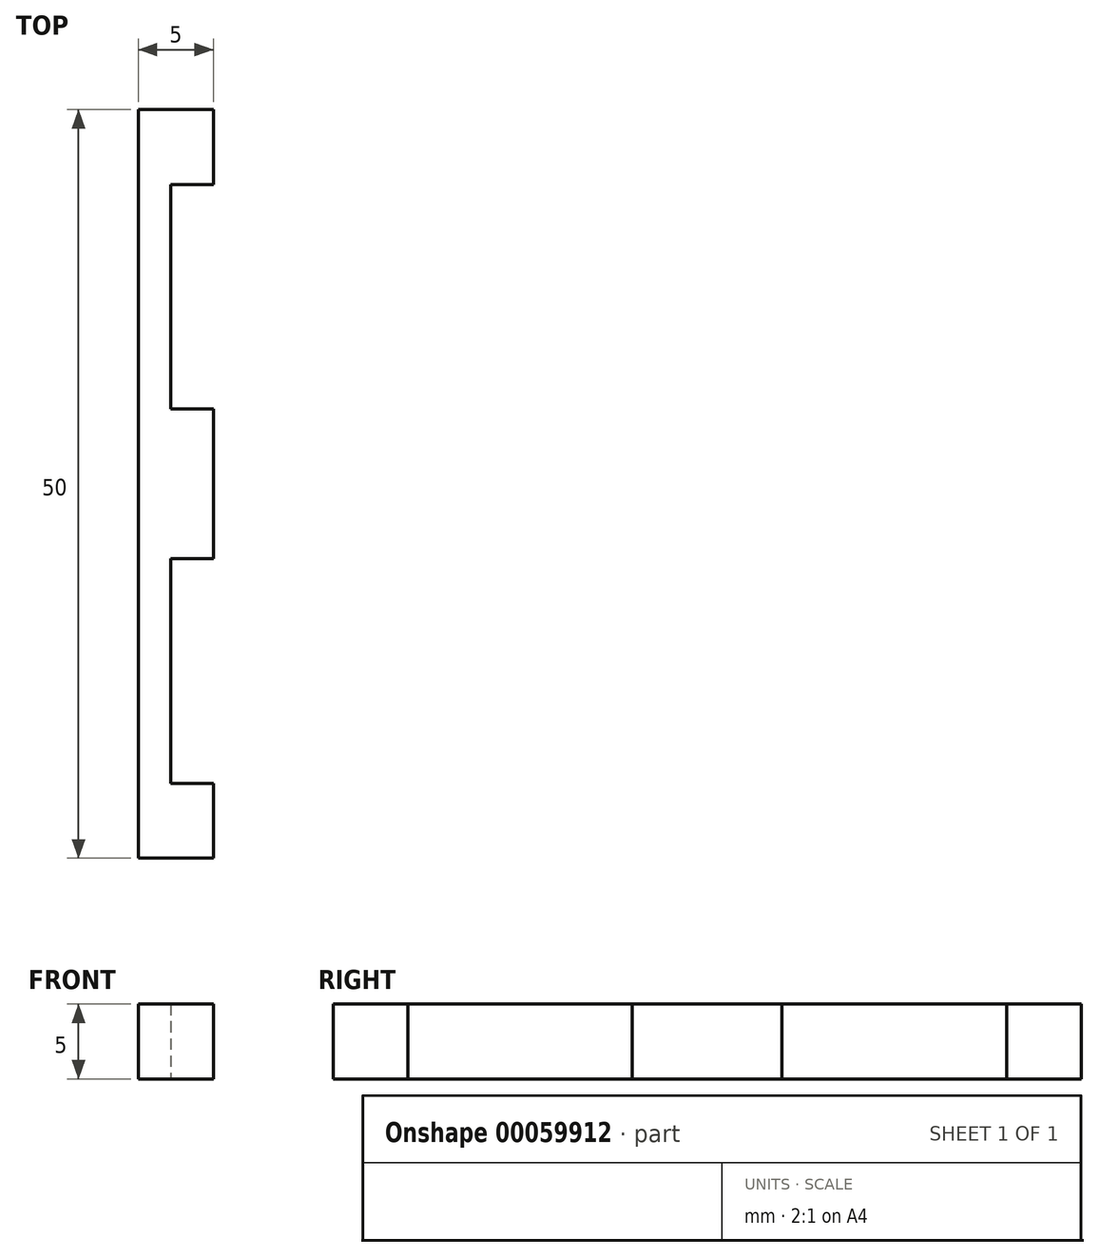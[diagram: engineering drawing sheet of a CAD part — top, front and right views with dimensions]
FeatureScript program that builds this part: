
annotation { "Feature Type Name" : "Feature", "Feature Type Description" : "" }
export const myFeature = defineFeature(function(context is Context, id is Id, definition is map)
    precondition{}
    {
        {
            var Q0;
            Q0=qCreatedBy(makeId("Right.planeOp"),FACE);
            var sketch = newSketch(context, id + "F0", { "sketchPlane" : qUnion([Q0])});
            skLineSegment(sketch, "E0.bottom", {"start": v(-32.42, 0.5) * mm, "end": v(17.58, 0.5) * mm});
            skLineSegment(sketch, "E0.top", {"start": v(-32.42, -4.5) * mm, "end": v(17.58, -4.5) * mm});
            skLineSegment(sketch, "E0.left", {"start": v(-32.42, 0.5) * mm, "end": v(-32.42, -4.5) * mm});
            skLineSegment(sketch, "E0.right", {"start": v(17.58, 0.5) * mm, "end": v(17.58, -4.5) * mm});
            skSolve(sketch);
        }
        {
            var Q0;
            Q0=makeQuery(id+"F0.imprint","IMPRINT",FACE,{"disambiguationData":[TD([[makeQuery(id+"F0.imprint","IMPRINT",EDGE,{"derivedFrom":sQuery(id+"F0.wireOp",EDGE,"E0.bottom")}),-1.0]])]});
            extrude(context, id + "F1", {"entities" : qUnion([Q0]), "depth" : 5 * mm, "offsetDistance" : 25 * mm});
        }
        {
            var Q0;
            Q0=makeQuery(id+"F1.opExtrude","SWEPT_FACE",FACE,{"disambiguationData":[OSD([sQuery(id+"F0.wireOp",EDGE,"E0.top")])]});
            var sketch = newSketch(context, id + "F2", { "sketchPlane" : qUnion([Q0])});
            skLineSegment(sketch, "E1.bottom", {"start": v(5, 27.42) * mm, "end": v(2.17, 27.42) * mm});
            skLineSegment(sketch, "E1.top", {"start": v(5, 12.42) * mm, "end": v(2.17, 12.42) * mm});
            skLineSegment(sketch, "E1.left", {"start": v(5, 27.42) * mm, "end": v(5, 12.42) * mm});
            skLineSegment(sketch, "E1.right", {"start": v(2.17, 27.42) * mm, "end": v(2.17, 12.42) * mm});
            skLineSegment(sketch, "E2.bottom", {"start": v(5, -12.58) * mm, "end": v(2.17, -12.58) * mm});
            skLineSegment(sketch, "E2.top", {"start": v(5, 2.42) * mm, "end": v(2.17, 2.42) * mm});
            skLineSegment(sketch, "E2.left", {"start": v(5, -12.58) * mm, "end": v(5, 2.42) * mm});
            skLineSegment(sketch, "E2.right", {"start": v(2.17, -12.58) * mm, "end": v(2.17, 2.42) * mm});
            skSolve(sketch);
        }
        {
            var Q0;
            Q0=makeQuery(id+"F2.imprint","IMPRINT",FACE,{"disambiguationData":[TD([[makeQuery(id+"F2.imprint","IMPRINT",EDGE,{"derivedFrom":sQuery(id+"F2.wireOp",EDGE,"E1.bottom")}),1.0]])]});
            var Q1;
            Q1=makeQuery(id+"F2.imprint","IMPRINT",FACE,{"disambiguationData":[TD([[makeQuery(id+"F2.imprint","IMPRINT",EDGE,{"derivedFrom":sQuery(id+"F2.wireOp",EDGE,"E2.bottom")}),-1.0]])]});
            extrude(context, id + "F3", {"entities" : qUnion([Q0, Q1]), "operationType" : NewBodyOperationType.REMOVE, "oppositeDirection" : true, "depth" : 5.1 * mm, "offsetDistance" : 25 * mm});
        }
    });
